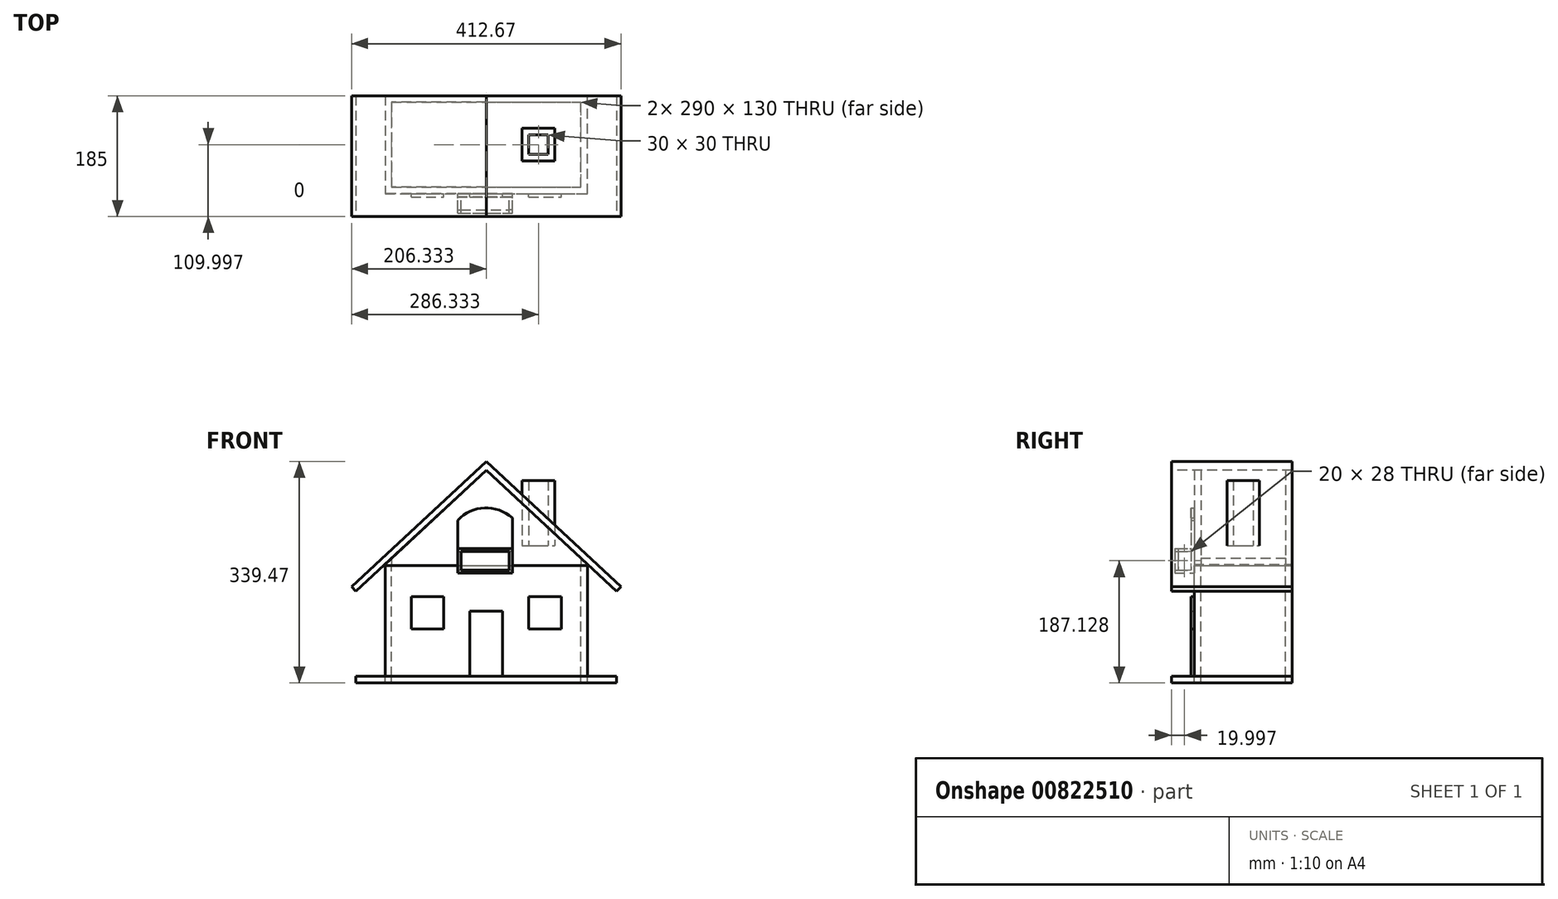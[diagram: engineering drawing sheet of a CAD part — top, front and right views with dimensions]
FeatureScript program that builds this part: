
annotation { "Feature Type Name" : "Feature", "Feature Type Description" : "" }
export const myFeature = defineFeature(function(context is Context, id is Id, definition is map)
    precondition{}
    {
        {
            var Q0;
            Q0=qCreatedBy(makeId("Top.planeOp"),FACE);
            var sketch = newSketch(context, id + "F0", { "sketchPlane" : qUnion([Q0])});
            skLineSegment(sketch, "E0.bottom", {"start": v(-57.99, -15.46) * mm, "end": v(252.01, -15.46) * mm});
            skLineSegment(sketch, "E0.top", {"start": v(-57.99, 134.54) * mm, "end": v(252.01, 134.54) * mm});
            skLineSegment(sketch, "E0.left", {"start": v(-57.99, -15.46) * mm, "end": v(-57.99, 134.54) * mm});
            skLineSegment(sketch, "E0.right", {"start": v(252.01, -15.46) * mm, "end": v(252.01, 134.54) * mm});
            skLineSegment(sketch, "E1.bottom", {"start": v(-47.99, -5.46) * mm, "end": v(242.01, -5.46) * mm});
            skLineSegment(sketch, "E1.top", {"start": v(-47.99, 124.54) * mm, "end": v(242.01, 124.54) * mm});
            skLineSegment(sketch, "E1.left", {"start": v(-47.99, -5.46) * mm, "end": v(-47.99, 124.54) * mm});
            skLineSegment(sketch, "E1.right", {"start": v(242.01, -5.46) * mm, "end": v(242.01, 124.54) * mm});
            skSolve(sketch);
        }
        {
            var Q0;
            Q0=makeQuery(id+"F0.imprint","IMPRINT",FACE,{"disambiguationData":[TD([[makeQuery(id+"F0.imprint","IMPRINT",EDGE,{"derivedFrom":sQuery(id+"F0.wireOp",EDGE,"E0.bottom")}),1.0]])]});
            extrude(context, id + "F1", {"entities" : qUnion([Q0]), "oppositeDirection" : true, "depth" : 170 * mm, "offsetDistance" : 25 * mm});
        }
        {
            var Q0;
            Q0=makeQuery(id+"F1.opExtrude","SWEPT_FACE",FACE,{"disambiguationData":[OSD([sQuery(id+"F0.wireOp",EDGE,"E0.bottom")])]});
            var sketch = newSketch(context, id + "F2", { "sketchPlane" : qUnion([Q0])});
            skLineSegment(sketch, "E2.bottom", {"start": v(72.01, -170) * mm, "end": v(122.01, -170) * mm});
            skLineSegment(sketch, "E2.top", {"start": v(72.01, -70) * mm, "end": v(122.01, -70) * mm});
            skLineSegment(sketch, "E2.left", {"start": v(72.01, -170) * mm, "end": v(72.01, -70) * mm});
            skLineSegment(sketch, "E2.right", {"start": v(122.01, -170) * mm, "end": v(122.01, -70) * mm});
            skLineSegment(sketch, "E3", {"start": v(97.01, 0) * mm, "end": v(97.01, 178.07) * mm, "construction": true});
            skLineSegment(sketch, "E4", {"start": v(-102.51, -39.62) * mm, "end": v(97.01, 145.82) * mm});
            skLineSegment(sketch, "E5", {"start": v(-102.51, -39.62) * mm, "end": v(-109.32, -32.3) * mm});
            skLineSegment(sketch, "E6", {"start": v(-109.32, -32.3) * mm, "end": v(97.01, 159.47) * mm});
            skLineSegment(sketch, "E7.MirrorCS", {"start": v(296.54, -39.62) * mm, "end": v(97.01, 145.82) * mm});
            skLineSegment(sketch, "E8.MirrorCS", {"start": v(303.35, -32.3) * mm, "end": v(97.01, 159.47) * mm});
            skLineSegment(sketch, "E9.MirrorCS", {"start": v(296.54, -39.62) * mm, "end": v(303.35, -32.3) * mm});
            skSolve(sketch);
        }
        {
            var Q0;
            Q0=makeQuery(id+"F2.imprint","IMPRINT",FACE,{"disambiguationData":[TD([[makeQuery(id+"F2.imprint","IMPRINT",EDGE,{"derivedFrom":sQuery(id+"F2.wireOp",EDGE,"E4")}),1.0]])]});
            extrude(context, id + "F3", {"entities" : qUnion([Q0]), "oppositeDirection" : true, "depth" : 150 * mm, "offsetDistance" : 25 * mm, "hasSecondDirection" : true, "secondDirectionOppositeDirection" : false, "secondDirectionDepth" : 35 * mm});
        }
        {
            var Q0;
            Q0=makeQuery(id+"F0.imprint","IMPRINT",FACE,{"disambiguationData":[TD([[makeQuery(id+"F0.imprint","IMPRINT",EDGE,{"derivedFrom":sQuery(id+"F0.wireOp",EDGE,"E0.bottom")}),1.0]])]});
            extrude(context, id + "F4", {"entities" : qUnion([Q0]), "endBound" : BoundingType.UP_TO_NEXT, "depth" : 25 * mm, "offsetDistance" : 25 * mm});
        }
        {
            var Q0;
            Q0=makeQuery(id+"F1.opExtrude","CAP_FACE",FACE,{"disambiguationData":[OSD([sQuery(id+"F0.wireOp",EDGE,"E0.bottom"),sQuery(id+"F0.wireOp",EDGE,"E0.top"),sQuery(id+"F0.wireOp",EDGE,"E0.left"),sQuery(id+"F0.wireOp",EDGE,"E0.right"),sQuery(id+"F0.wireOp",EDGE,"E1.bottom"),sQuery(id+"F0.wireOp",EDGE,"E1.top"),sQuery(id+"F0.wireOp",EDGE,"E1.left"),sQuery(id+"F0.wireOp",EDGE,"E1.right")])],"isStart":false});
            var sketch = newSketch(context, id + "F5", { "sketchPlane" : qUnion([Q0])});
            skLineSegment(sketch, "E10.bottom", {"start": v(152.01, -34.54) * mm, "end": v(202.01, -34.54) * mm});
            skLineSegment(sketch, "E10.top", {"start": v(152.01, -84.54) * mm, "end": v(202.01, -84.54) * mm});
            skLineSegment(sketch, "E10.left", {"start": v(152.01, -34.54) * mm, "end": v(152.01, -84.54) * mm});
            skLineSegment(sketch, "E10.right", {"start": v(202.01, -34.54) * mm, "end": v(202.01, -84.54) * mm});
            skLineSegment(sketch, "E11.bottom", {"start": v(162.01, -44.54) * mm, "end": v(192.01, -44.54) * mm});
            skLineSegment(sketch, "E11.top", {"start": v(162.01, -74.54) * mm, "end": v(192.01, -74.54) * mm});
            skLineSegment(sketch, "E11.left", {"start": v(162.01, -44.54) * mm, "end": v(162.01, -74.54) * mm});
            skLineSegment(sketch, "E11.right", {"start": v(192.01, -44.54) * mm, "end": v(192.01, -74.54) * mm});
            skSolve(sketch);
        }
        {
            var Q0;
            Q0=makeQuery(id+"F5.imprint","IMPRINT",FACE,{"disambiguationData":[TD([[makeQuery(id+"F5.imprint","IMPRINT",EDGE,{"derivedFrom":sQuery(id+"F5.wireOp",EDGE,"E10.bottom")}),-1.0]])]});
            extrude(context, id + "F6", {"entities" : qUnion([Q0]), "oppositeDirection" : true, "depth" : 300 * mm, "offsetDistance" : 25 * mm, "hasSecondDirection" : true, "secondDirectionOppositeDirection" : false, "secondDirectionDepth" : -200 * mm});
        }
        {
            var Q0;
            Q0=makeQuery(id+"F2.imprint","IMPRINT",FACE,{"disambiguationData":[TD([[makeQuery(id+"F2.imprint","IMPRINT",EDGE,{"derivedFrom":sQuery(id+"F2.wireOp",EDGE,"E2.top")}),1.0]])]});
            var sketch = newSketch(context, id + "F7", { "sketchPlane" : qUnion([Q0])});
            skLineSegment(sketch, "E12", {"start": v(53.34, 69.06) * mm, "end": v(53.34, -11.87) * mm});
            skLineSegment(sketch, "E13", {"start": v(137.01, 72.7) * mm, "end": v(137.01, -11.87) * mm});
            skLineSegment(sketch, "E14", {"start": v(53.34, -11.87) * mm, "end": v(137.01, -11.87) * mm});
            skArc(sketch, "E15", {"start": v(137.01, 72.7) * mm, "mid": v(94.43, 88.07) * mm, "end": v(53.34, 69.06) * mm});
            skLineSegment(sketch, "E16", {"start": v(97.01, 88.13) * mm, "end": v(97.01, -11.87) * mm});
            skLineSegment(sketch, "E17.bottom", {"start": v(-17.99, -47.63) * mm, "end": v(32.01, -47.63) * mm});
            skLineSegment(sketch, "E17.top", {"start": v(-17.99, -97.63) * mm, "end": v(32.01, -97.63) * mm});
            skLineSegment(sketch, "E17.left", {"start": v(-17.99, -47.63) * mm, "end": v(-17.99, -97.63) * mm});
            skLineSegment(sketch, "E17.right", {"start": v(32.01, -47.63) * mm, "end": v(32.01, -97.63) * mm});
            skLineSegment(sketch, "E18.bottom", {"start": v(162.01, -47.63) * mm, "end": v(212.01, -47.63) * mm});
            skLineSegment(sketch, "E18.top", {"start": v(162.01, -97.63) * mm, "end": v(212.01, -97.63) * mm});
            skLineSegment(sketch, "E18.left", {"start": v(162.01, -47.63) * mm, "end": v(162.01, -97.63) * mm});
            skLineSegment(sketch, "E18.right", {"start": v(212.01, -47.63) * mm, "end": v(212.01, -97.63) * mm});
            skSolve(sketch);
        }
        {
            var Q0;
            Q0=makeQuery(id+"F7.imprint","IMPRINT",FACE,{"disambiguationData":[TD([[makeQuery(id+"F7.imprint","IMPRINT",EDGE,{"derivedFrom":sQuery(id+"F7.wireOp",EDGE,"E17.bottom")}),-1.0]])]});
            var Q1;
            Q1=makeQuery(id+"F7.imprint","IMPRINT",FACE,{"disambiguationData":[TD([[makeQuery(id+"F7.imprint","IMPRINT",EDGE,{"derivedFrom":sQuery(id+"F7.wireOp",EDGE,"E18.bottom")}),-1.0]])]});
            extrude(context, id + "F8", {"entities" : qUnion([Q0, Q1]), "depth" : 5 * mm, "offsetDistance" : 25 * mm});
        }
        {
            var Q0;
            {var subQ0=sQuery(id+"F7.wireOp",EDGE,"E15");var subQ1=sQuery(id+"F7.wireOp",EDGE,"E12");var subQ2=makeQuery(id+"F7.imprint","INTERSECT",VERTEX,{"derivedFrom":[subQ1,subQ0]});Q0=makeQuery(id+"F7.imprint","IMPRINT",FACE,{"disambiguationData":[TD([[makeQuery(id+"F7.imprint","IMPRINT",EDGE,{"disambiguationData":[TD([[subQ2,-1.0]])],"derivedFrom":subQ1}),1.0]])]});}
            var Q1;
            {var subQ0=sQuery(id+"F7.wireOp",EDGE,"E14");var subQ1=sQuery(id+"F7.wireOp",EDGE,"E12");var subQ2=makeQuery(id+"F7.imprint","INTERSECT",VERTEX,{"derivedFrom":[subQ1,subQ0]});Q1=makeQuery(id+"F7.imprint","IMPRINT",FACE,{"disambiguationData":[TD([[makeQuery(id+"F7.imprint","IMPRINT",EDGE,{"disambiguationData":[TD([[subQ2,1.0]])],"derivedFrom":subQ1}),1.0]])]});}
            var Q2;
            {var subQ0=sQuery(id+"F7.wireOp",EDGE,"E14");var subQ1=sQuery(id+"F7.wireOp",EDGE,"E13");var subQ2=makeQuery(id+"F7.imprint","INTERSECT",VERTEX,{"derivedFrom":[subQ1,subQ0]});Q2=makeQuery(id+"F7.imprint","IMPRINT",FACE,{"disambiguationData":[TD([[makeQuery(id+"F7.imprint","IMPRINT",EDGE,{"disambiguationData":[TD([[subQ2,1.0]])],"derivedFrom":subQ1}),-1.0]])]});}
            var Q3;
            {var subQ0=sQuery(id+"F7.wireOp",EDGE,"E15");var subQ1=sQuery(id+"F7.wireOp",EDGE,"E13");var subQ2=makeQuery(id+"F7.imprint","INTERSECT",VERTEX,{"derivedFrom":[subQ1,subQ0]});Q3=makeQuery(id+"F7.imprint","IMPRINT",FACE,{"disambiguationData":[TD([[makeQuery(id+"F7.imprint","IMPRINT",EDGE,{"disambiguationData":[TD([[subQ2,-1.0]])],"derivedFrom":subQ1}),-1.0]])]});}
            extrude(context, id + "F9", {"entities" : qUnion([Q0, Q1, Q2, Q3]), "depth" : 5 * mm, "offsetDistance" : 25 * mm});
        }
        {
            var Q0;
            Q0=makeQuery(id+"F9.opExtrude","CAP_FACE",FACE,{"disambiguationData":[OSD([sQuery(id+"F7.wireOp",EDGE,"E12"),sQuery(id+"F7.wireOp",EDGE,"E13"),sQuery(id+"F7.wireOp",EDGE,"E14"),sQuery(id+"F7.wireOp",EDGE,"E15")])],"isStart":false});
            var sketch = newSketch(context, id + "F10", { "sketchPlane" : qUnion([Q0])});
            skLineSegment(sketch, "E19.bottom", {"start": v(53.34, -6.87) * mm, "end": v(137.01, -6.87) * mm});
            skLineSegment(sketch, "E19.top", {"start": v(53.34, -11.87) * mm, "end": v(137.01, -11.87) * mm});
            skLineSegment(sketch, "E19.left", {"start": v(53.34, -6.87) * mm, "end": v(53.34, -11.87) * mm});
            skLineSegment(sketch, "E19.right", {"start": v(137.01, -6.87) * mm, "end": v(137.01, -11.87) * mm});
            skSolve(sketch);
        }
        {
            var Q0;
            Q0=makeQuery(id+"F10.imprint","IMPRINT",FACE,{"disambiguationData":[TD([[makeQuery(id+"F10.imprint","IMPRINT",EDGE,{"derivedFrom":sQuery(id+"F10.wireOp",EDGE,"E19.bottom")}),-1.0]])]});
            extrude(context, id + "F11", {"entities" : qUnion([Q0]), "operationType" : NewBodyOperationType.ADD, "depth" : 25 * mm, "offsetDistance" : 25 * mm});
        }
        {
            var Q0;
            Q0=makeQuery(id+"F11.opExtrude","SWEPT_FACE",FACE,{"disambiguationData":[OSD([sQuery(id+"F10.wireOp",EDGE,"E19.bottom")])]});
            var sketch = newSketch(context, id + "F12", { "sketchPlane" : qUnion([Q0])});
            skLineSegment(sketch, "E20.bottom", {"start": v(53.34, -45.46) * mm, "end": v(58.34, -45.46) * mm});
            skLineSegment(sketch, "E20.top", {"start": v(53.34, -40.46) * mm, "end": v(58.34, -40.46) * mm});
            skLineSegment(sketch, "E20.left", {"start": v(53.34, -45.46) * mm, "end": v(53.34, -40.46) * mm});
            skLineSegment(sketch, "E20.right", {"start": v(58.34, -45.46) * mm, "end": v(58.34, -40.46) * mm});
            skLineSegment(sketch, "E21.bottom", {"start": v(137.01, -45.46) * mm, "end": v(132.01, -45.46) * mm});
            skLineSegment(sketch, "E21.top", {"start": v(137.01, -40.46) * mm, "end": v(132.01, -40.46) * mm});
            skLineSegment(sketch, "E21.left", {"start": v(137.01, -45.46) * mm, "end": v(137.01, -40.46) * mm});
            skLineSegment(sketch, "E21.right", {"start": v(132.01, -45.46) * mm, "end": v(132.01, -40.46) * mm});
            skSolve(sketch);
        }
        {
            var Q0;
            Q0=makeQuery(id+"F12.imprint","IMPRINT",FACE,{"disambiguationData":[TD([[makeQuery(id+"F12.imprint","IMPRINT",EDGE,{"derivedFrom":sQuery(id+"F12.wireOp",EDGE,"E20.bottom")}),1.0]])]});
            var Q1;
            Q1=makeQuery(id+"F12.imprint","IMPRINT",FACE,{"disambiguationData":[TD([[makeQuery(id+"F12.imprint","IMPRINT",EDGE,{"derivedFrom":sQuery(id+"F12.wireOp",EDGE,"E21.bottom")}),1.0]])]});
            extrude(context, id + "F13", {"entities" : qUnion([Q0, Q1]), "operationType" : NewBodyOperationType.ADD, "depth" : 28 * mm, "offsetDistance" : 25 * mm});
        }
        {
            var Q0;
            Q0=makeQuery(id+"F13.opExtrude","CAP_FACE",FACE,{"disambiguationData":[OSD([sQuery(id+"F12.wireOp",EDGE,"E20.bottom"),sQuery(id+"F12.wireOp",EDGE,"E20.top"),sQuery(id+"F12.wireOp",EDGE,"E20.left"),sQuery(id+"F12.wireOp",EDGE,"E20.right")])],"isStart":false});
            var sketch = newSketch(context, id + "F14", { "sketchPlane" : qUnion([Q0])});
            skPoint(sketch, "E22.0", {"position": v(137.01, -40.46) * mm});
            skLineSegment(sketch, "E23.bottom", {"start": v(53.34, -45.46) * mm, "end": v(137.01, -45.46) * mm});
            skLineSegment(sketch, "E23.top", {"start": v(53.34, -40.46) * mm, "end": v(137.01, -40.46) * mm});
            skLineSegment(sketch, "E23.left", {"start": v(53.34, -45.46) * mm, "end": v(53.34, -40.46) * mm});
            skLineSegment(sketch, "E23.right", {"start": v(137.01, -45.46) * mm, "end": v(137.01, -40.46) * mm});
            skLineSegment(sketch, "E24.bottom", {"start": v(137.01, -45.46) * mm, "end": v(132.01, -45.46) * mm});
            skLineSegment(sketch, "E24.top", {"start": v(137.01, -20.46) * mm, "end": v(132.01, -20.46) * mm});
            skLineSegment(sketch, "E24.left", {"start": v(137.01, -45.46) * mm, "end": v(137.01, -20.46) * mm});
            skLineSegment(sketch, "E24.right", {"start": v(132.01, -45.46) * mm, "end": v(132.01, -20.46) * mm});
            skLineSegment(sketch, "E25.bottom", {"start": v(53.34, -45.46) * mm, "end": v(58.34, -45.46) * mm});
            skLineSegment(sketch, "E25.top", {"start": v(53.34, -20.46) * mm, "end": v(58.34, -20.46) * mm});
            skLineSegment(sketch, "E25.left", {"start": v(53.34, -45.46) * mm, "end": v(53.34, -20.46) * mm});
            skLineSegment(sketch, "E25.right", {"start": v(58.34, -45.46) * mm, "end": v(58.34, -20.46) * mm});
            skSolve(sketch);
        }
        {
            var Q0;
            {var subQ5=sQuery(id+"F14.wireOp",EDGE,"E24.top");Q0=makeQuery(id+"F14.imprint","IMPRINT",FACE,{"disambiguationData":[TD([[makeQuery(id+"F14.imprint","IMPRINT",EDGE,{"derivedFrom":subQ5}),1.0]])]});}
            var Q1;
            {var subQ5=sQuery(id+"F14.wireOp",EDGE,"E24.bottom");Q1=makeQuery(id+"F14.imprint","IMPRINT",FACE,{"disambiguationData":[TD([[makeQuery(id+"F14.imprint","IMPRINT",EDGE,{"derivedFrom":subQ5}),-1.0]])]});}
            var Q2;
            {var subQ0=sQuery(id+"F14.wireOp",EDGE,"E23.bottom");Q2=makeQuery(id+"F14.imprint","IMPRINT",FACE,{"disambiguationData":[TD([[makeQuery(id+"F14.imprint","IMPRINT",EDGE,{"derivedFrom":subQ0}),1.0]])]});}
            var Q3;
            {var subQ5=sQuery(id+"F14.wireOp",EDGE,"E25.bottom");Q3=makeQuery(id+"F14.imprint","IMPRINT",FACE,{"disambiguationData":[TD([[makeQuery(id+"F14.imprint","IMPRINT",EDGE,{"derivedFrom":subQ5}),1.0]])]});}
            var Q4;
            {var subQ5=sQuery(id+"F14.wireOp",EDGE,"E25.top");Q4=makeQuery(id+"F14.imprint","IMPRINT",FACE,{"disambiguationData":[TD([[makeQuery(id+"F14.imprint","IMPRINT",EDGE,{"derivedFrom":subQ5}),-1.0]])]});}
            extrude(context, id + "F15", {"entities" : qUnion([Q0, Q1, Q2, Q3, Q4]), "operationType" : NewBodyOperationType.ADD, "depth" : 5 * mm, "offsetDistance" : 25 * mm});
        }
        {
            var Q0;
            Q0=makeQuery(id+"F2.imprint","IMPRINT",FACE,{"disambiguationData":[TD([[makeQuery(id+"F2.imprint","IMPRINT",EDGE,{"derivedFrom":sQuery(id+"F2.wireOp",EDGE,"E2.bottom")}),1.0]])]});
            extrude(context, id + "F16", {"entities" : qUnion([Q0]), "depth" : 5 * mm, "offsetDistance" : 25 * mm});
        }
        {
            var Q0;
            Q0=makeQuery(id+"F5.imprint","IMPRINT",FACE,{"disambiguationData":[TD([[makeQuery(id+"F5.imprint","IMPRINT",EDGE,{"derivedFrom":makeQuery(id+"F1.opExtrude","CAP_EDGE",EDGE,{"disambiguationData":[OSD([sQuery(id+"F0.wireOp",EDGE,"E0.bottom")])],"isStart":false})}),-1.0]])]});
            var sketch = newSketch(context, id + "F17", { "sketchPlane" : qUnion([Q0])});
            skPoint(sketch, "E26.0", {"position": v(-102.51, -134.54) * mm});
            skPoint(sketch, "E27.0", {"position": v(296.54, 50.46) * mm});
            skLineSegment(sketch, "E28.bottom", {"start": v(-102.51, -134.54) * mm, "end": v(296.54, -134.54) * mm});
            skLineSegment(sketch, "E28.top", {"start": v(-102.51, 50.46) * mm, "end": v(296.54, 50.46) * mm});
            skLineSegment(sketch, "E28.left", {"start": v(-102.51, -134.54) * mm, "end": v(-102.51, 50.46) * mm});
            skLineSegment(sketch, "E28.right", {"start": v(296.54, -134.54) * mm, "end": v(296.54, 50.46) * mm});
            skSolve(sketch);
        }
        {
            var Q0;
            Q0=makeQuery(id+"F17.imprint","IMPRINT",FACE,{"disambiguationData":[TD([[makeQuery(id+"F17.imprint","IMPRINT",EDGE,{"derivedFrom":sQuery(id+"F17.wireOp",EDGE,"E28.top")}),-1.0]])]});
            var Q1;
            Q1=makeQuery(id+"F17.imprint","IMPRINT",FACE,{"disambiguationData":[TD([[makeQuery(id+"F17.imprint","IMPRINT",EDGE,{"derivedFrom":makeQuery(id+"F5.imprint","IMPRINT",EDGE,{"derivedFrom":makeQuery(id+"F1.opExtrude","CAP_EDGE",EDGE,{"disambiguationData":[OSD([sQuery(id+"F0.wireOp",EDGE,"E1.bottom")])],"isStart":false})})}),-1.0]])]});
            var Q2;
            Q2=makeQuery(id+"F5.imprint","IMPRINT",FACE,{"disambiguationData":[TD([[makeQuery(id+"F5.imprint","IMPRINT",EDGE,{"derivedFrom":makeQuery(id+"F1.opExtrude","CAP_EDGE",EDGE,{"disambiguationData":[OSD([sQuery(id+"F0.wireOp",EDGE,"E0.bottom")])],"isStart":false})}),-1.0]])]});
            extrude(context, id + "F18", {"entities" : qUnion([Q0, Q1, Q2]), "depth" : 10 * mm, "offsetDistance" : 25 * mm});
        }
    });
